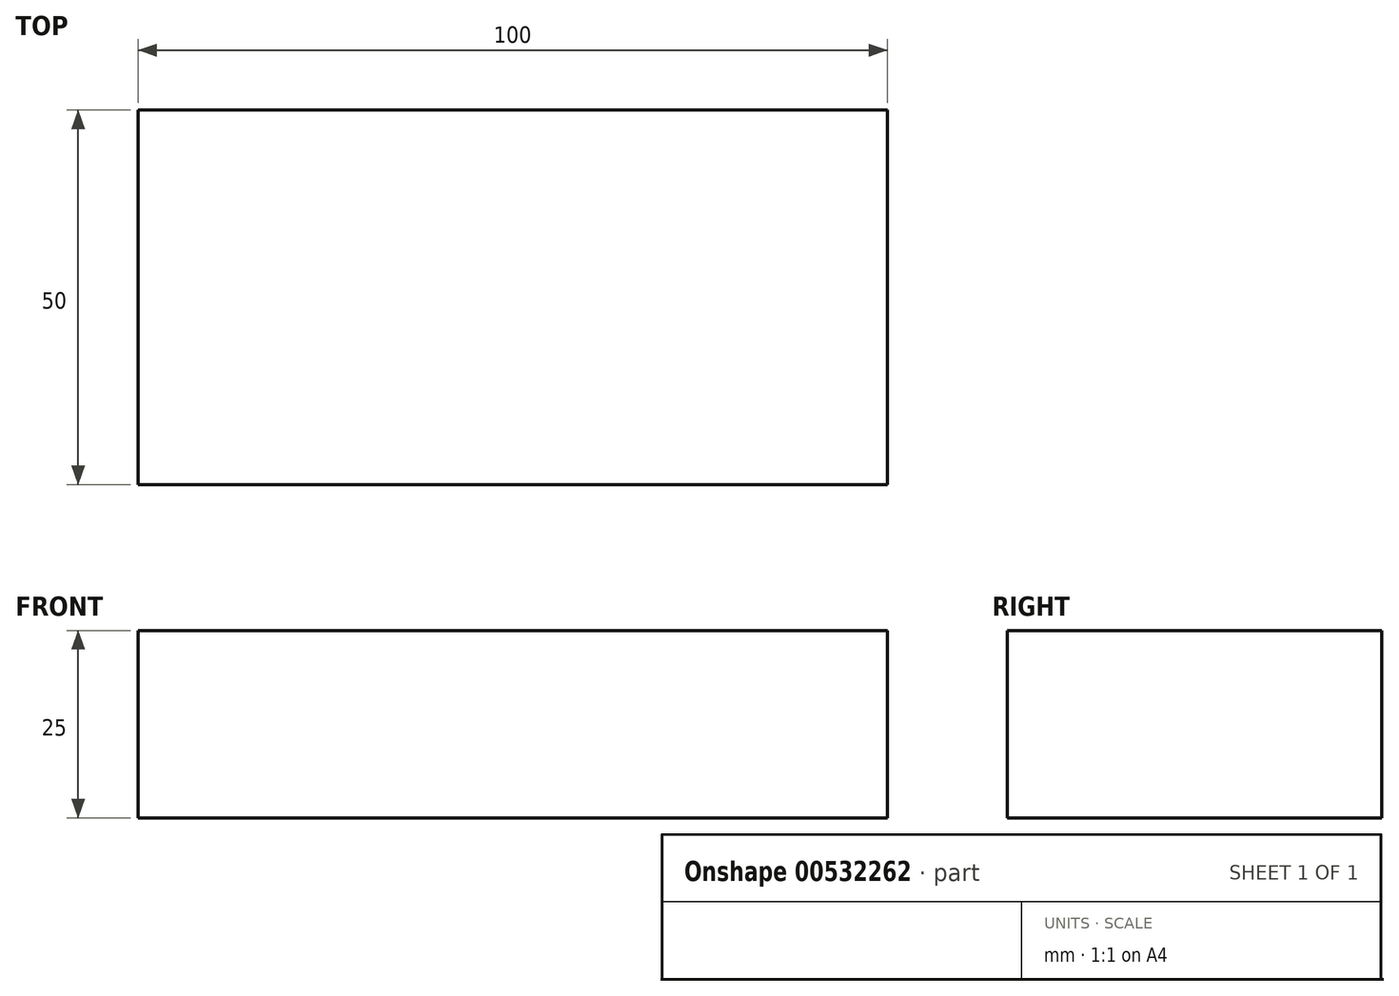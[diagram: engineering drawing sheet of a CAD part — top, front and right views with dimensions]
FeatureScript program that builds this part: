
annotation { "Feature Type Name" : "Feature", "Feature Type Description" : "" }
export const myFeature = defineFeature(function(context is Context, id is Id, definition is map)
    precondition{}
    {
        {
            var Q0;
            Q0=qCreatedBy(makeId("Top.planeOp"),FACE);
            var sketch = newSketch(context, id + "F0", { "sketchPlane" : qUnion([Q0])});
            skLineSegment(sketch, "E0.bottom", {"start": v(-50, 25) * mm, "end": v(50, 25) * mm});
            skLineSegment(sketch, "E0.top", {"start": v(-50, -25) * mm, "end": v(50, -25) * mm});
            skLineSegment(sketch, "E0.left", {"start": v(-50, 25) * mm, "end": v(-50, -25) * mm});
            skLineSegment(sketch, "E0.right", {"start": v(50, 25) * mm, "end": v(50, -25) * mm});
            skPoint(sketch, "E0.middle", {"position": v(0, 0) * mm});
            skSolve(sketch);
        }
        {
            var Q0;
            Q0=makeQuery(id+"F0.imprint","IMPRINT",FACE,{"disambiguationData":[TD([[makeQuery(id+"F0.imprint","IMPRINT",EDGE,{"derivedFrom":sQuery(id+"F0.wireOp",EDGE,"E0.bottom")}),-1.0]])]});
            extrude(context, id + "F1", {"entities" : qUnion([Q0]), "depth" : 25 * mm, "offsetDistance" : 25 * mm});
        }
    });
